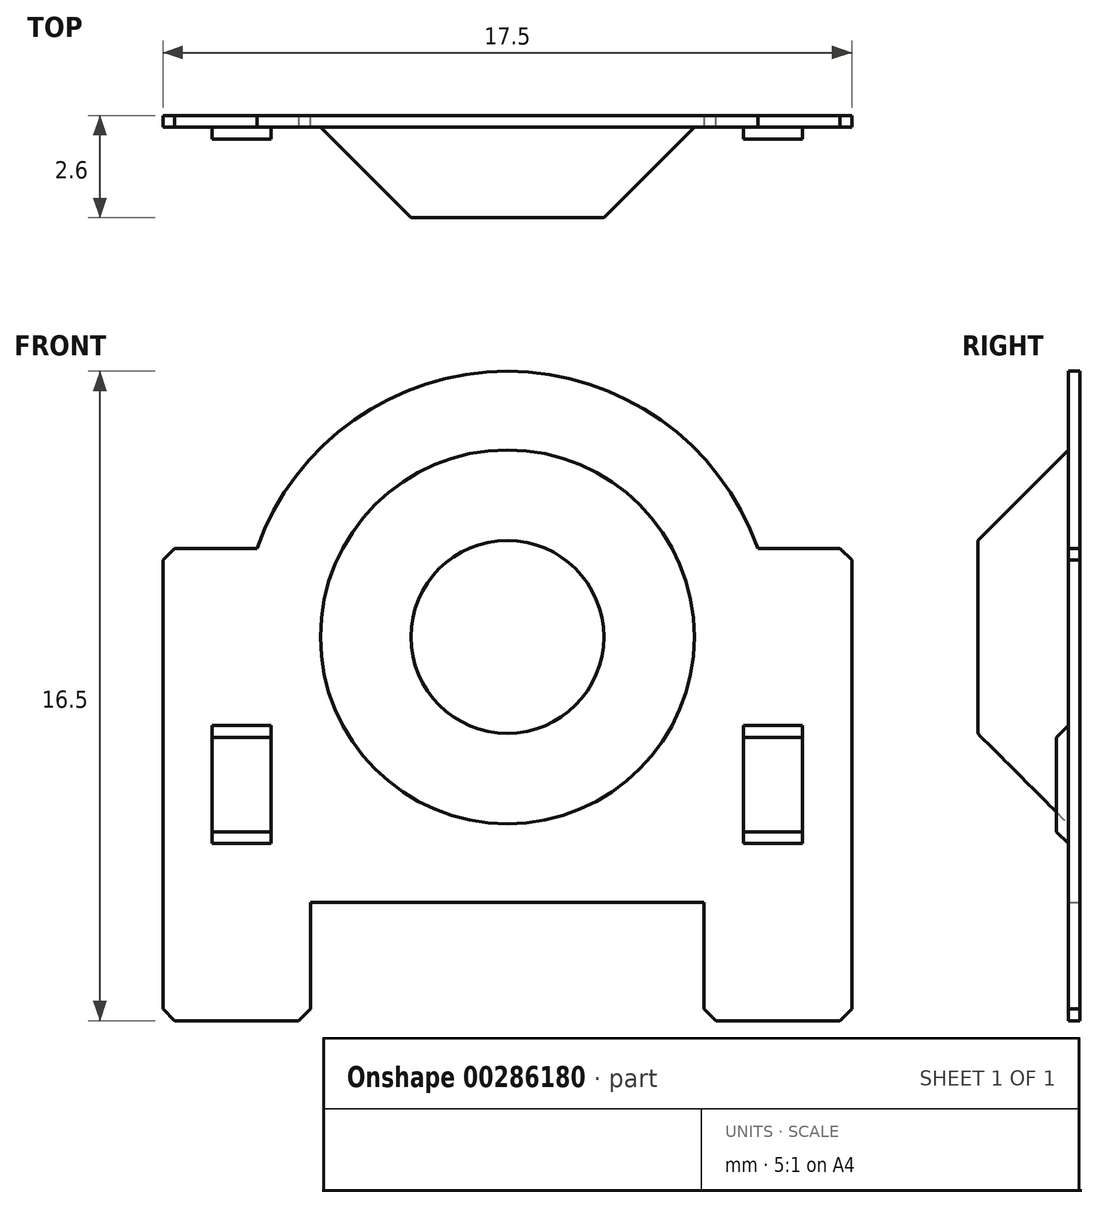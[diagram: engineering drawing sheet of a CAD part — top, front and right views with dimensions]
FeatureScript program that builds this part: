
annotation { "Feature Type Name" : "Feature", "Feature Type Description" : "" }
export const myFeature = defineFeature(function(context is Context, id is Id, definition is map)
    precondition{}
    {
        {
            var Q0;
            Q0=qCreatedBy(makeId("Front.planeOp"),FACE);
            var sketch = newSketch(context, id + "F0", { "sketchPlane" : qUnion([Q0])});
            skLineSegment(sketch, "E0.bottom", {"start": v(8.75, 6) * mm, "end": v(6.36, 6) * mm});
            skLineSegment(sketch, "E0.top", {"start": v(8.75, -6) * mm, "end": v(5, -6) * mm});
            skLineSegment(sketch, "E0.left", {"start": v(8.75, 6) * mm, "end": v(8.75, -6) * mm});
            skLineSegment(sketch, "E0.right", {"start": v(-8.75, 6) * mm, "end": v(-8.75, -6) * mm});
            skPoint(sketch, "E0.middle", {"position": v(0, 0) * mm});
            skLineSegment(sketch, "E1.top", {"start": v(-5, -3) * mm, "end": v(5, -3) * mm});
            skLineSegment(sketch, "E1.left", {"start": v(-5, -6) * mm, "end": v(-5, -3) * mm});
            skLineSegment(sketch, "E1.right", {"start": v(5, -6) * mm, "end": v(5, -3) * mm});
            skLineSegment(sketch, "E2.trimOffspring", {"start": v(-5, -6) * mm, "end": v(-8.75, -6) * mm});
            skArc(sketch, "E3", {"start": v(6.36, 6) * mm, "mid": v(0, 10.5) * mm, "end": v(-6.36, 6) * mm});
            skPoint(sketch, "E3.centerSnap0", {"position": v(0, -3) * mm});
            skLineSegment(sketch, "E4.trimOffspring", {"start": v(-6.36, 6) * mm, "end": v(-8.75, 6) * mm});
            skLineSegment(sketch, "E5.bottom", {"start": v(-6, -1.5) * mm, "end": v(-7.5, -1.5) * mm});
            skLineSegment(sketch, "E5.top", {"start": v(-6, 1.5) * mm, "end": v(-7.5, 1.5) * mm});
            skLineSegment(sketch, "E5.left", {"start": v(-6, -1.5) * mm, "end": v(-6, 1.5) * mm});
            skLineSegment(sketch, "E5.right", {"start": v(-7.5, -1.5) * mm, "end": v(-7.5, 1.5) * mm});
            skPoint(sketch, "E5.middle", {"position": v(-6.75, 0) * mm});
            skLineSegment(sketch, "E6.bottom", {"start": v(7.5, -1.5) * mm, "end": v(6, -1.5) * mm});
            skLineSegment(sketch, "E6.top", {"start": v(7.5, 1.5) * mm, "end": v(6, 1.5) * mm});
            skLineSegment(sketch, "E6.left", {"start": v(7.5, -1.5) * mm, "end": v(7.5, 1.5) * mm});
            skLineSegment(sketch, "E6.right", {"start": v(6, -1.5) * mm, "end": v(6, 1.5) * mm});
            skPoint(sketch, "E6.middle", {"position": v(6.75, 0) * mm});
            skSolve(sketch);
        }
        {
            var Q0;
            Q0=makeQuery(id+"F0.imprint","IMPRINT",FACE,{"disambiguationData":[TD([[makeQuery(id+"F0.imprint","IMPRINT",EDGE,{"derivedFrom":sQuery(id+"F0.wireOp",EDGE,"E0.bottom")}),1.0]])]});
            var Q1;
            Q1=makeQuery(id+"F0.imprint","IMPRINT",FACE,{"disambiguationData":[TD([[makeQuery(id+"F0.imprint","IMPRINT",EDGE,{"derivedFrom":sQuery(id+"F0.wireOp",EDGE,"E5.bottom")}),-1.0]])]});
            var Q2;
            Q2=makeQuery(id+"F0.imprint","IMPRINT",FACE,{"disambiguationData":[TD([[makeQuery(id+"F0.imprint","IMPRINT",EDGE,{"derivedFrom":sQuery(id+"F0.wireOp",EDGE,"E6.bottom")}),-1.0]])]});
            extrude(context, id + "F1", {"entities" : qUnion([Q0, Q1, Q2]), "depth" : .3 * mm});
        }
        {
            var Q0;
            Q0=makeQuery(id+"F0.imprint","IMPRINT",FACE,{"disambiguationData":[TD([[makeQuery(id+"F0.imprint","IMPRINT",EDGE,{"derivedFrom":sQuery(id+"F0.wireOp",EDGE,"E5.bottom")}),-1.0]])]});
            var Q1;
            Q1=makeQuery(id+"F0.imprint","IMPRINT",FACE,{"disambiguationData":[TD([[makeQuery(id+"F0.imprint","IMPRINT",EDGE,{"derivedFrom":sQuery(id+"F0.wireOp",EDGE,"E6.bottom")}),-1.0]])]});
            extrude(context, id + "F2", {"entities" : qUnion([Q0, Q1]), "operationType" : NewBodyOperationType.ADD, "depth" : .6 * mm});
        }
        {
            var Q0;
            Q0=makeQuery(id+"F1.opExtrude","CAP_FACE",FACE,{"disambiguationData":[OSD([sQuery(id+"F0.wireOp",EDGE,"E0.bottom"),sQuery(id+"F0.wireOp",EDGE,"E0.top"),sQuery(id+"F0.wireOp",EDGE,"E0.left"),sQuery(id+"F0.wireOp",EDGE,"E0.right"),sQuery(id+"F0.wireOp",EDGE,"E1.top"),sQuery(id+"F0.wireOp",EDGE,"E1.left"),sQuery(id+"F0.wireOp",EDGE,"E1.right"),sQuery(id+"F0.wireOp",EDGE,"E2.trimOffspring"),sQuery(id+"F0.wireOp",EDGE,"E3"),sQuery(id+"F0.wireOp",EDGE,"E4.trimOffspring")])],"isStart":false});
            var sketch = newSketch(context, id + "F3", { "sketchPlane" : qUnion([Q0])});
            skCircle(sketch, "E7", {"center": v(0, 3.75) * mm, "radius": 4.75 * mm});
            skSolve(sketch);
        }
        {
            var Q0;
            Q0=makeQuery(id+"F3.imprint","IMPRINT",FACE,{"disambiguationData":[TD([[makeQuery(id+"F3.imprint","IMPRINT",EDGE,{"derivedFrom":sQuery(id+"F3.wireOp",EDGE,"E7")}),1.0]])]});
            extrude(context, id + "F4", {"entities" : qUnion([Q0]), "operationType" : NewBodyOperationType.ADD, "depth" : 2.3 * mm});
        }
        {
            var Q0;
            Q0=makeQuery(id+"F4.opExtrude","CAP_EDGE",EDGE,{"disambiguationData":[OSD([sQuery(id+"F3.wireOp",EDGE,"E7")])],"isStart":false});
            chamfer(context, id + "F5", {"entities" : qUnion([Q0]), "width" : 2.3 * mm, "tangentPropagation" : true});
        }
        {
            var Q0;
            Q0=makeQuery(id+"F2.opExtrude","CAP_EDGE",EDGE,{"disambiguationData":[OSD([sQuery(id+"F0.wireOp",EDGE,"E5.bottom")])],"isStart":false});
            var Q1;
            Q1=makeQuery(id+"F2.opExtrude","CAP_EDGE",EDGE,{"disambiguationData":[OSD([sQuery(id+"F0.wireOp",EDGE,"E5.top")])],"isStart":false});
            var Q2;
            Q2=makeQuery(id+"F2.opExtrude","CAP_EDGE",EDGE,{"disambiguationData":[OSD([sQuery(id+"F0.wireOp",EDGE,"E6.bottom")])],"isStart":false});
            var Q3;
            Q3=makeQuery(id+"F2.opExtrude","CAP_EDGE",EDGE,{"disambiguationData":[OSD([sQuery(id+"F0.wireOp",EDGE,"E6.top")])],"isStart":false});
            var Q4;
            Q4=makeQuery(id+"F1.opExtrude","SWEPT_EDGE",EDGE,{"disambiguationData":[OSD([sQuery(id+"F0.wireOp",EDGE,"E1.left"),sQuery(id+"F0.wireOp",EDGE,"E2.trimOffspring")])]});
            var Q5;
            Q5=makeQuery(id+"F1.opExtrude","SWEPT_EDGE",EDGE,{"disambiguationData":[OSD([sQuery(id+"F0.wireOp",EDGE,"E0.right"),sQuery(id+"F0.wireOp",EDGE,"E2.trimOffspring")])]});
            var Q6;
            Q6=makeQuery(id+"F1.opExtrude","SWEPT_EDGE",EDGE,{"disambiguationData":[OSD([sQuery(id+"F0.wireOp",EDGE,"E0.top"),sQuery(id+"F0.wireOp",EDGE,"E1.right")])]});
            var Q7;
            Q7=makeQuery(id+"F1.opExtrude","SWEPT_EDGE",EDGE,{"disambiguationData":[OSD([sQuery(id+"F0.wireOp",EDGE,"E0.top"),sQuery(id+"F0.wireOp",EDGE,"E0.left")])]});
            var Q8;
            Q8=makeQuery(id+"F1.opExtrude","SWEPT_EDGE",EDGE,{"disambiguationData":[OSD([sQuery(id+"F0.wireOp",EDGE,"E0.bottom"),sQuery(id+"F0.wireOp",EDGE,"E0.left")])]});
            var Q9;
            Q9=makeQuery(id+"F1.opExtrude","SWEPT_EDGE",EDGE,{"disambiguationData":[OSD([sQuery(id+"F0.wireOp",EDGE,"E0.right"),sQuery(id+"F0.wireOp",EDGE,"E4.trimOffspring")])]});
            chamfer(context, id + "F6", {"entities" : qUnion([Q0, Q1, Q2, Q3, Q4, Q5, Q6, Q7, Q8, Q9]), "width" : .3 * mm, "tangentPropagation" : true});
        }
    });
